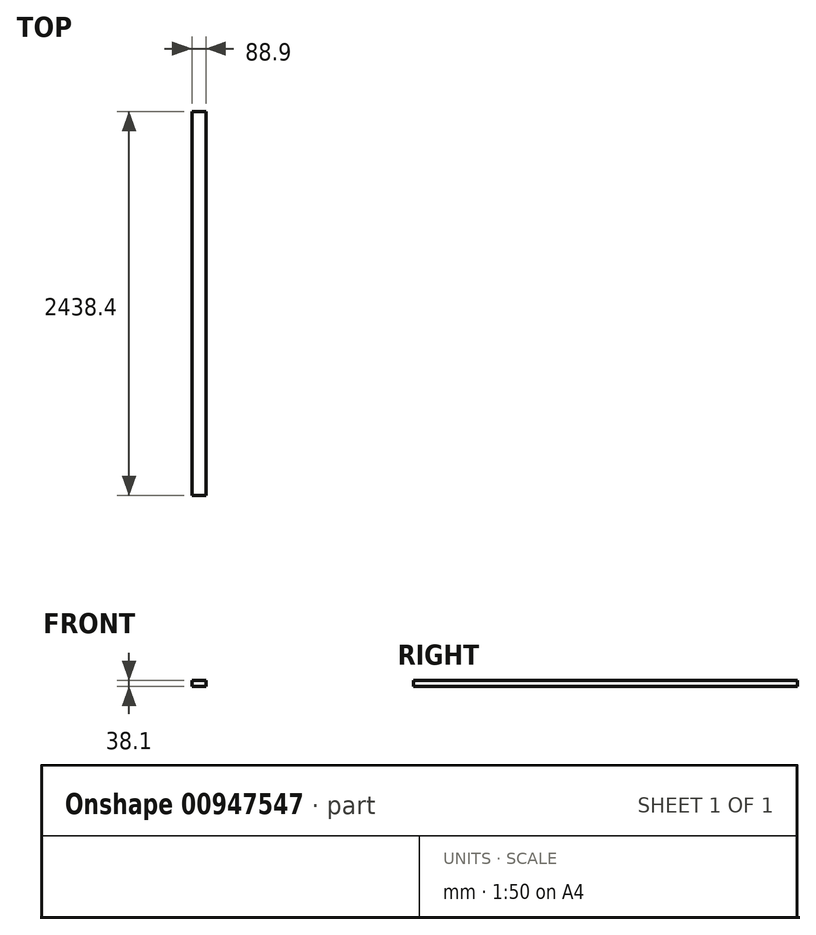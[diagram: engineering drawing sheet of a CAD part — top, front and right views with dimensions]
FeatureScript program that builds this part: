
annotation { "Feature Type Name" : "Feature", "Feature Type Description" : "" }
export const myFeature = defineFeature(function(context is Context, id is Id, definition is map)
    precondition{}
    {
        {
            var Q0;
            Q0=qCreatedBy(makeId("Front.planeOp"),FACE);
            var sketch = newSketch(context, id + "F0", { "sketchPlane" : qUnion([Q0])});
            skLineSegment(sketch, "E0.bottom", {"start": v(44.45, 19.05) * mm, "end": v(-44.45, 19.05) * mm});
            skLineSegment(sketch, "E0.top", {"start": v(44.45, -19.05) * mm, "end": v(-44.45, -19.05) * mm});
            skLineSegment(sketch, "E0.left", {"start": v(44.45, 19.05) * mm, "end": v(44.45, -19.05) * mm});
            skLineSegment(sketch, "E0.right", {"start": v(-44.45, 19.05) * mm, "end": v(-44.45, -19.05) * mm});
            skPoint(sketch, "E0.middle", {"position": v(0, 0) * mm});
            skSolve(sketch);
        }
        {
            var Q0;
            Q0=makeQuery(id+"F0.imprint","IMPRINT",FACE,{"disambiguationData":[TD([[makeQuery(id+"F0.imprint","IMPRINT",EDGE,{"derivedFrom":sQuery(id+"F0.wireOp",EDGE,"E0.bottom")}),1.0]])]});
            var Q1;
            Q1=sQuery(id+"F0.wireOp",EDGE,"E0.bottom");
            var Q2;
            Q2=sQuery(id+"F0.wireOp",EDGE,"E0.left");
            var Q3;
            Q3=sQuery(id+"F0.wireOp",EDGE,"E0.top");
            var Q4;
            Q4=sQuery(id+"F0.wireOp",EDGE,"E0.right");
            extrude(context, id + "F1", {"entities" : qUnion([Q0]), "surfaceEntities" : qUnion([Q1, Q2, Q3, Q4]), "endBound" : BoundingType.SYMMETRIC, "depth" : 2438.4 * mm, "offsetDistance" : 25.4 * mm});
        }
    });
